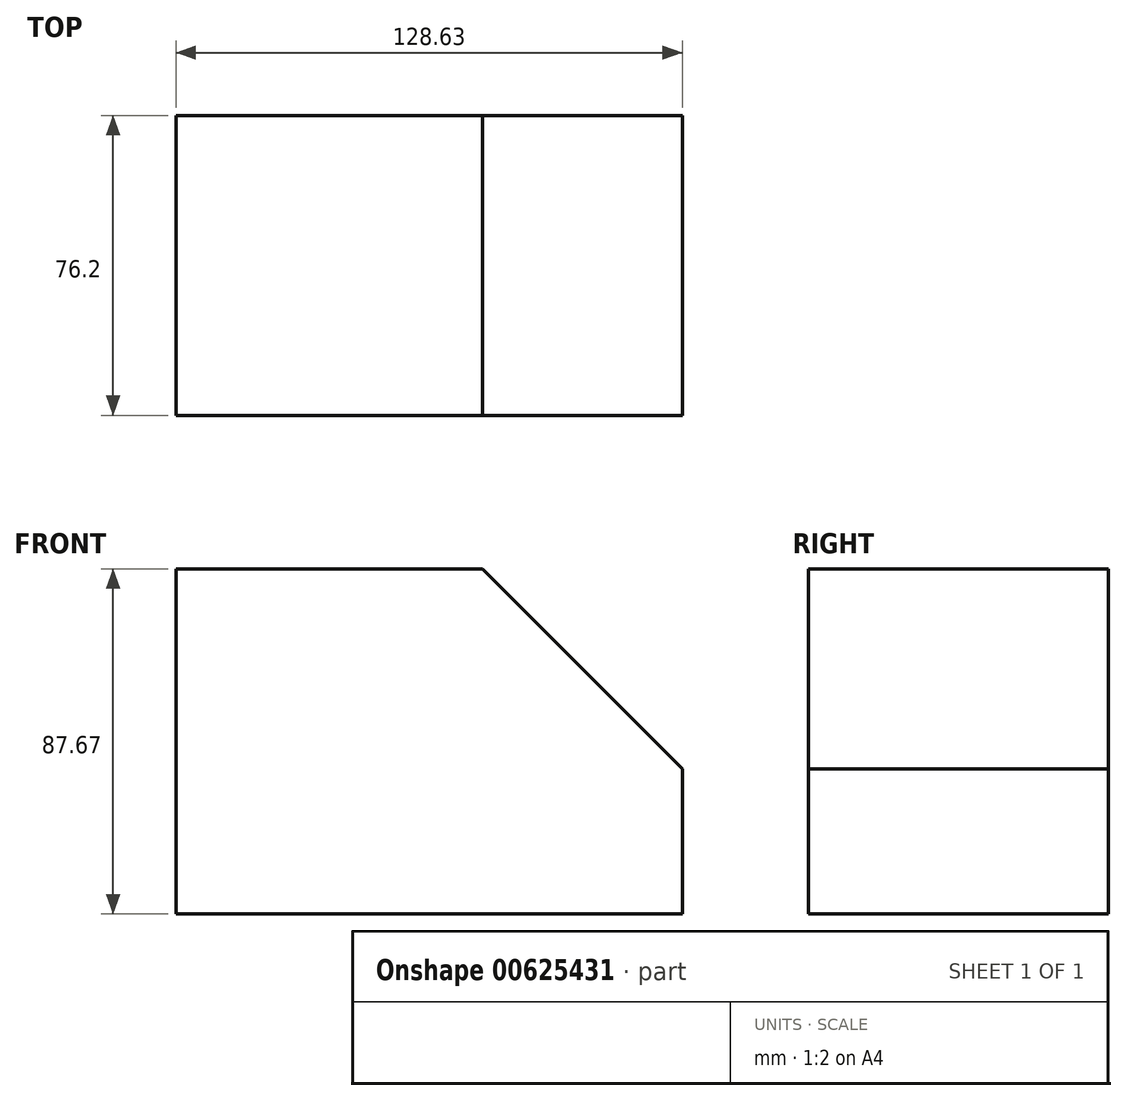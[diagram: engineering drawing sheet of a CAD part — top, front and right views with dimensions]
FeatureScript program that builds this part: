
annotation { "Feature Type Name" : "Feature", "Feature Type Description" : "" }
export const myFeature = defineFeature(function(context is Context, id is Id, definition is map)
    precondition{}
    {
        {
            var Q0;
            Q0=qCreatedBy(makeId("Front.planeOp"),FACE);
            var sketch = newSketch(context, id + "F0", { "sketchPlane" : qUnion([Q0])});
            skLineSegment(sketch, "E0.bottom", {"start": v(-60.82, 38.57) * mm, "end": v(67.8, 38.57) * mm});
            skLineSegment(sketch, "E0.top", {"start": v(-60.82, -49.1) * mm, "end": v(67.8, -49.1) * mm});
            skLineSegment(sketch, "E0.left", {"start": v(-60.82, 38.57) * mm, "end": v(-60.82, -49.1) * mm});
            skLineSegment(sketch, "E0.right", {"start": v(67.8, 38.57) * mm, "end": v(67.8, -49.1) * mm});
            skSolve(sketch);
        }
        {
            var Q0;
            Q0=makeQuery(id+"F0.imprint","IMPRINT",FACE,{"disambiguationData":[TD([[makeQuery(id+"F0.imprint","IMPRINT",EDGE,{"derivedFrom":sQuery(id+"F0.wireOp",EDGE,"E0.bottom")}),-1.0]])]});
            extrude(context, id + "F1", {"entities" : qUnion([Q0]), "depth" : 76.2 * mm, "offsetDistance" : 25.4 * mm});
        }
        {
            var Q0;
            Q0=makeQuery(id+"F1.opExtrude","SWEPT_EDGE",EDGE,{"disambiguationData":[OSD([sQuery(id+"F0.wireOp",EDGE,"E0.bottom"),sQuery(id+"F0.wireOp",EDGE,"E0.right")])]});
            chamfer(context, id + "F2", {"entities" : qUnion([Q0]), "width" : 50.8 * mm, "tangentPropagation" : true});
        }
    });
